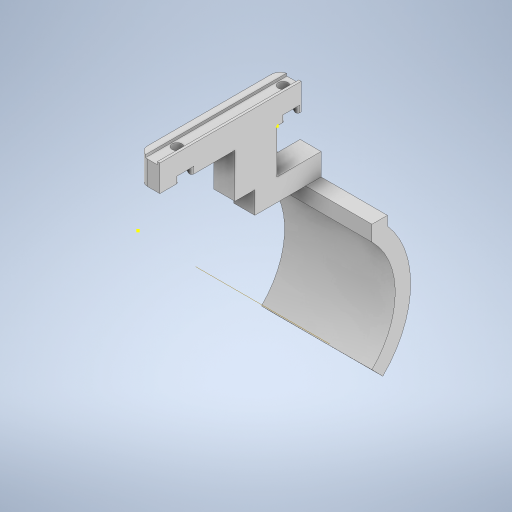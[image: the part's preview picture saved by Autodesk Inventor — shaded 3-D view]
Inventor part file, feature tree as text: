
AUTODESK INVENTOR PART (.ipt)
format: ipt  version: 2024 (Build 280153000, 153)  size: 391,680 bytes
history: native  units: in
note: dims shown in document units (in); Inventor stores cm internally (conversion verified against a paired STEP export)
features: sketch x11, extrude x6, projected_geometry x4, fillet x2, sweep x1, other x1, revolve x1
ambient origin geometry x8: Origin, YZ Plane, XZ Plane, XY Plane, X Axis, Y Axis, Z Axis, Center Point
bodies: Solid1 (feature_tree)
feature tree (26):
  extrude  "Extrusion1"  Depth=2.5197in
  extrude  "Extrusion2"  Depth=1.8898in
  extrude  "Extrusion3"  Depth=0.4724in TaperAngle=0.0deg
  fillet  "Fillet1"  Radius=0.0433in
  fillet  "Fillet2"  Radius=0.2126in
  extrude  "Extrusion19"  Depth=0.4724in TaperAngle=0.0deg
  extrude  "Extrusion21"  Depth=0.1181in TaperAngle=0.0deg
  sketch  "Sketch41"  dims[d17=0.1772in d18=0.0394in]
  extrude  "Extrusion22"  Depth=0.0394in
  sweep  "Sweep3"
  other  "Work Axis1"
  revolve  "Revolution1"  [1 undecoded]
  sketch  "Sketch47"  dims[d131=1.1811in d132=0.3937in d133=0.0in d134=1.1811in d135=0.2756in d137=1.9685in d138=0.2756in d139=0.0in d142=1.9685in d143=1.378in d144=0.0in d145=0.0in d146=90.0deg d42=0.0197in d43=0.0344in d44=0.0197in d45=0.0344in d46=0.0in d47=0.0in d48=0.0in d49=0.0in d50=0.0in d51=0.0in d52=0.0in d53=0.0in d55=0.0197in d56=0.0344in d57=0.0197in d58=0.0344in d60=0.0197in d61=0.0344in d62=0.0197in d63=0.0344in d72=0.0197in d73=0.0344in d74=0.0197in d75=0.0344in d140=0.0197in d141=0.0344in]
  sketch  "Sketch1"  dims[d1=0.374in d2=2.5197in]
  sketch  "Sketch2"  dims[d3=0.1772in d4=1.8898in]
  sketch  "Sketch3"  dims[d6=0.1457in d7=0.4724in d8=0.0in d9=0.0433in d10=0.2126in]
  projected_geometry  "Projected Loop2"
  projected_geometry  "Projected Loop3"
  projected_geometry  "Projected Loop4"
  projected_geometry  "Projected Loop5"
  sketch  "Sketch28"  dims[d11=0.0472in d12=0.4724in d13=0.0in]
  sketch  "Sketch40"  dims[d14=0.2953in d15=0.1181in d16=0.0in]
  sketch  "Sketch42"  dims[d19=0.1575in d76=0.4724in]
  sketch  "Sketch44"  dims[d107=0.102in d108=0.748in]
  sketch  "Sketch45"  dims[d109=0.7874in d110=0.0in]
  sketch  "Sketch46"  dims[d130=0.7874in]
note: 1 required parameter value undecoded (feature->parameter linkage not recoverable at this tier; creation-order binding heuristic only, values carry confidence <= 0.55)
